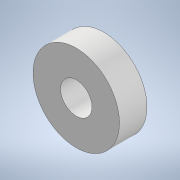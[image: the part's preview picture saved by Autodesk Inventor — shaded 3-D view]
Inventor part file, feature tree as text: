
AUTODESK INVENTOR PART (.ipt)
format: ipt  version: 2022 (Build 260153000, 153)  size: 97,792 bytes
history: native  units: in
note: dims shown in document units (in); Inventor stores cm internally (conversion verified against a paired STEP export)
features: extrude x1, sketch x1
ambient origin geometry x8: Origin, YZ Plane, XZ Plane, XY Plane, X Axis, Y Axis, Z Axis, Center Point
bodies: Solid1 (feature_tree)
feature tree (2):
  extrude  "Extrusion1"  Depth=0.2756in
  sketch  "Sketch1"  dims[d0=0.315in d1=0.8661in d2=0.2756in d3=0.0in]
